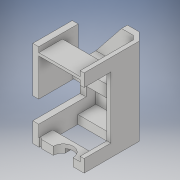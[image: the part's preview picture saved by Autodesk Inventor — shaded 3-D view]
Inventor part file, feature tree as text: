
AUTODESK INVENTOR PART (.ipt)
format: ipt  version: 2018 (Build 220112000, 112)  size: 153,088 bytes
history: native  units: in
note: dims shown in document units (in); Inventor stores cm internally (conversion verified against a paired STEP export)
features: other x3, sketch x1
ambient origin geometry x8: Origin, YZ Plane, XZ Plane, XY Plane, X Axis, Y Axis, Z Axis, Center Point
bodies: Solid1 (feature_tree)
feature tree (4):
  other  "Basev3.3.ipt"
  other  "Solid1::Basev3.3.ipt"
  other  "TaggingFeature1"
  sketch  "Sketch14"  dims[d0=0.3937in]
